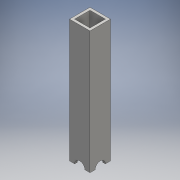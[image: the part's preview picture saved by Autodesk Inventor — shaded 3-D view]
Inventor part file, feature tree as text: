
AUTODESK INVENTOR PART (.ipt)
format: ipt  version: 2016 (Build 200138000, 138)  size: 113,664 bytes
history: native  units: mm
features: sketch x4, extrude x2, hole x2
ambient origin geometry x8: Origin, YZ Plane, XZ Plane, XY Plane, X Axis, Y Axis, Z Axis, Center Point
bodies: Solid1 (feature_tree)
feature tree (8):
  extrude  "Extrusion1"  Depth=16.0mm
  extrude  "Extrusion2"  Depth=12.0mm
  hole  "Hole7"  [1 undecoded]
  hole  "Hole8"  [1 undecoded]
  sketch  "Sketch1"  dims[d0=16.0mm d1=16.0mm]
  sketch  "Sketch2"  dims[d2=96.0mm d3=0.0mm d4=12.0mm]
  sketch  "Sketch9"  dims[d5=12.0mm d6=96.0mm d7=0.0mm]
  sketch  "Sketch10"  dims[d52=8.0mm d53=8.0mm d54=6.0mm d55=4.0mm d56=2.0mm d57=90.0deg d58=8.0mm d59=20.594885mm d60=8.0mm d61=8.0mm d62=6.0mm d63=4.0mm d64=2.0mm d65=90.0deg d66=8.0mm d67=20.594885mm]
note: 2 required parameter values undecoded (feature->parameter linkage not recoverable at this tier; creation-order binding heuristic only, values carry confidence <= 0.55)
